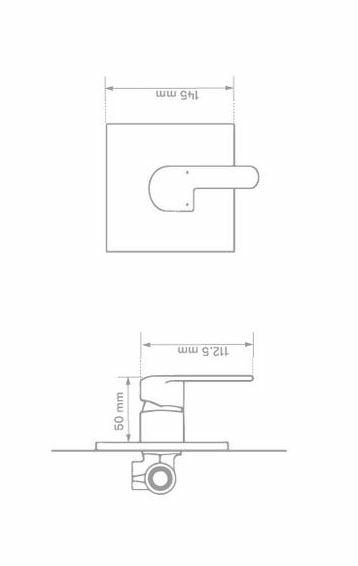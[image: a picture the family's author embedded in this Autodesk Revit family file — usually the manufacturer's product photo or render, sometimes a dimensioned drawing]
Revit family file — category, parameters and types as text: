
# Revit family: 01-1433-11 REGISTRO DUCHA COLECCION TOSCANA
name_source: partatom
category: Plumbing Fixtures
revit_build: Autodesk Revit 2018 (Build: 20170223_1515(x64)
units: mm (PartAtom-declared; Revit-internal decimal feet)

## family parameters
Cut with Voids When Loaded = No
Host = Face
OmniClass Number = 23.31.11.00
Part Type = Normal
Room Calculation Point = No
Round Connector Dimension = Use Diameter
Shared = No

## types (1)
- 01-1433-11
    Alto = 85 mm  [stored 0.278871 ft]
    Ancho manija = 70 mm
    CW Connection = Yes
    Default Elevation = 0 mm  [stored 0 ft]
    Description = Registro
    Dim escudo = 60 mm
    HW Connection = Yes
    Link Ficha Tecnica = http://infotecnica.gricol.com
    Manufacturer = Gricol
    Model = 01-1433-11
    Plastico - ABS Cromado = Plastico - ABS Cromado
    Product Name = REGISTRO DUCHA COLECCION TOSCANA
    Type Image = REGISTRO DUCHA COLECCION TOSCANA.JPG
    URL = https://www.gricol.com
    Vent Connection = No
    Waste Connection = No

note: [stored X ft] marks values corroborated as IEEE doubles in the binary element streams (Revit-internal decimal feet)

## geometry (parser evidence)
native form markers: Blend x2, Sweep x5
no freeform markers — native parametric forms only
